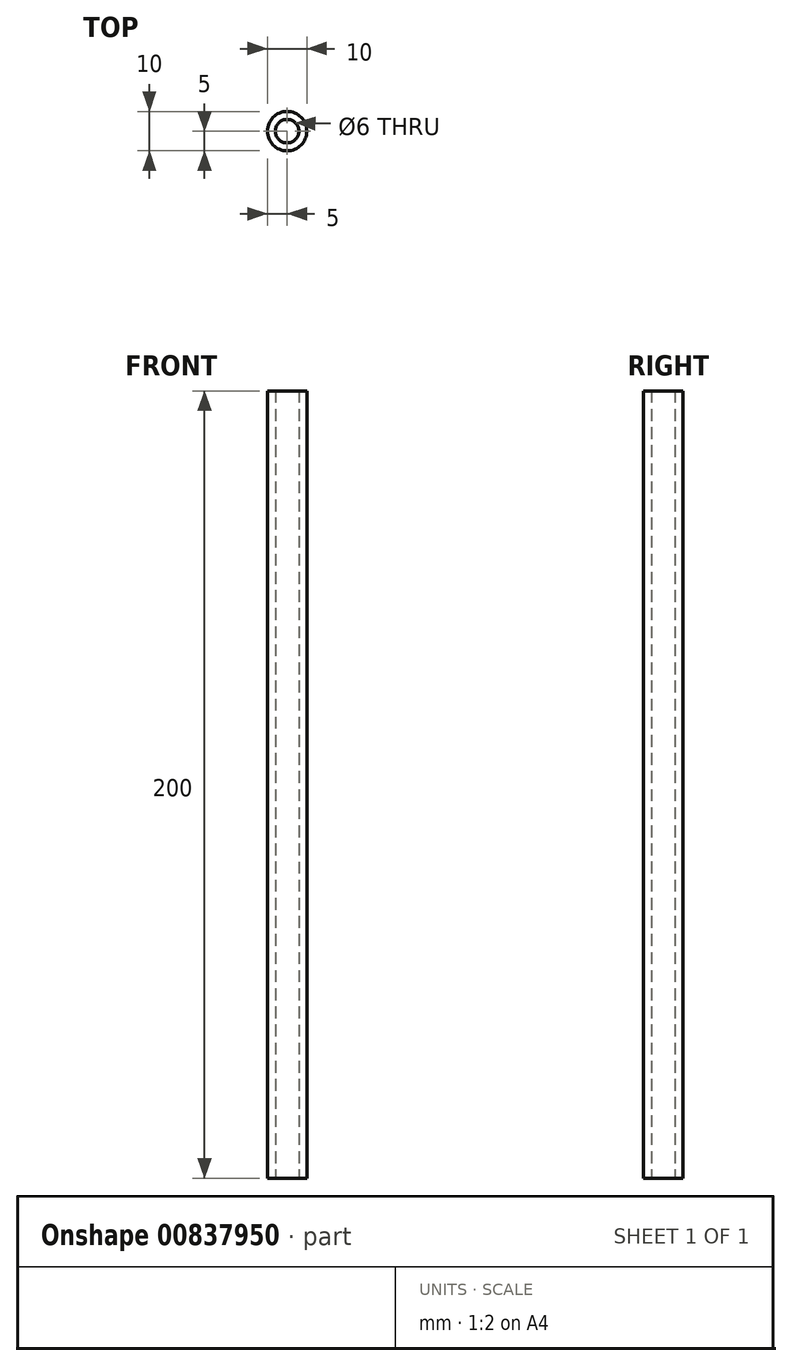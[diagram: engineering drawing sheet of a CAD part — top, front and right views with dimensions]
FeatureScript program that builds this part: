
annotation { "Feature Type Name" : "Feature", "Feature Type Description" : "" }
export const myFeature = defineFeature(function(context is Context, id is Id, definition is map)
    precondition{}
    {
        {
            var Q0;
            Q0=qCreatedBy(makeId("Top.planeOp"),FACE);
            var sketch = newSketch(context, id + "F0", { "sketchPlane" : qUnion([Q0])});
            skCircle(sketch, "E0", {"center": v(0, 0) * mm, "radius": 3 * mm});
            skCircle(sketch, "E1", {"center": v(0, 0) * mm, "radius": 5 * mm});
            skSolve(sketch);
        }
        {
            var Q0;
            Q0=makeQuery(id+"F0.imprint","IMPRINT",FACE,{"disambiguationData":[TD([[makeQuery(id+"F0.imprint","IMPRINT",EDGE,{"derivedFrom":sQuery(id+"F0.wireOp",EDGE,"E0")}),-1.0]])]});
            extrude(context, id + "F1", {"entities" : qUnion([Q0]), "depth" : 200 * mm, "offsetDistance" : 25 * mm});
        }
    });
